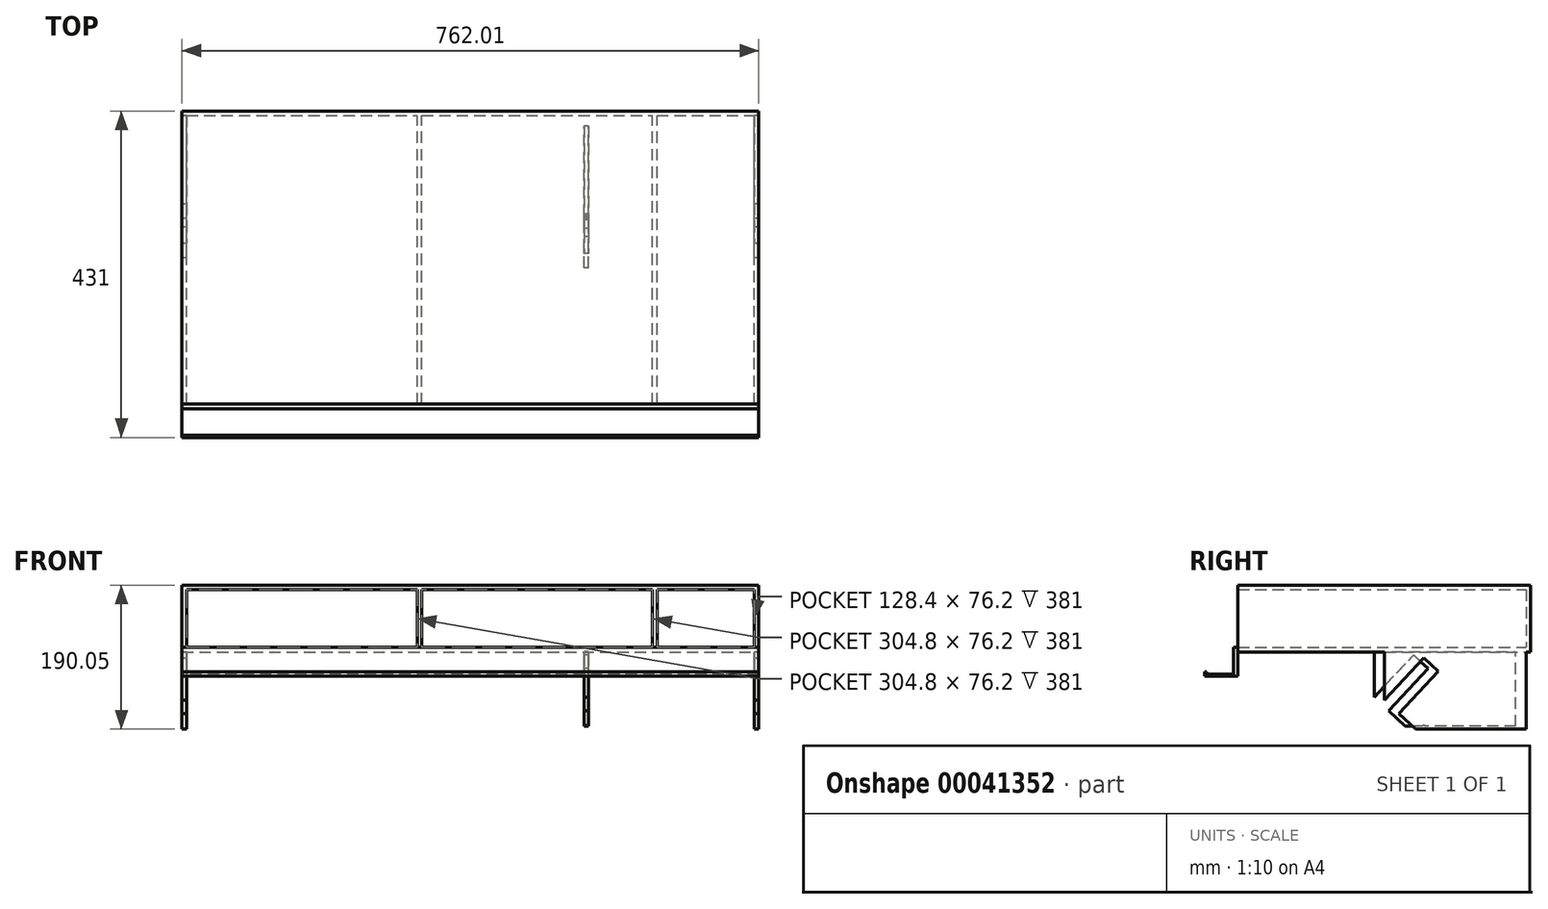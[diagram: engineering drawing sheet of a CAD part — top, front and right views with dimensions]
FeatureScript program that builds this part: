
annotation { "Feature Type Name" : "Feature", "Feature Type Description" : "" }
export const myFeature = defineFeature(function(context is Context, id is Id, definition is map)
    precondition{}
    {
        {
            var Q0;
            Q0=qCreatedBy(makeId("Front.planeOp"),FACE);
            var sketch = newSketch(context, id + "F0", { "sketchPlane" : qUnion([Q0])});
            skLineSegment(sketch, "E0.bottom", {"start": v(-621.6, 86.08) * mm, "end": v(140.4, 86.08) * mm});
            skLineSegment(sketch, "E0.left", {"start": v(-621.6, 86.08) * mm, "end": v(-621.6, 80.08) * mm});
            skLineSegment(sketch, "E0.right", {"start": v(140.4, 86.08) * mm, "end": v(140.4, 80.08) * mm});
            skLineSegment(sketch, "E1.bottom", {"start": v(-621.6, 80.08) * mm, "end": v(-615.6, 80.08) * mm});
            skLineSegment(sketch, "E1.top", {"start": v(-621.6, 3.88) * mm, "end": v(-615.6, 3.88) * mm});
            skLineSegment(sketch, "E1.left", {"start": v(-621.6, 80.08) * mm, "end": v(-621.6, 3.88) * mm});
            skLineSegment(sketch, "E1.right", {"start": v(-615.6, 80.08) * mm, "end": v(-615.6, 3.88) * mm});
            skLineSegment(sketch, "E2.bottom", {"start": v(-621.6, 3.88) * mm, "end": v(140.4, 3.88) * mm});
            skLineSegment(sketch, "E2.top", {"start": v(-621.6, -2.12) * mm, "end": v(140.4, -2.12) * mm});
            skLineSegment(sketch, "E2.left", {"start": v(-621.6, 3.88) * mm, "end": v(-621.6, -2.12) * mm});
            skLineSegment(sketch, "E2.right", {"start": v(140.4, 3.88) * mm, "end": v(140.4, -2.12) * mm});
            skLineSegment(sketch, "E3.bottom", {"start": v(140.4, 80.08) * mm, "end": v(134.4, 80.08) * mm});
            skLineSegment(sketch, "E3.top", {"start": v(140.4, 3.88) * mm, "end": v(134.4, 3.88) * mm});
            skLineSegment(sketch, "E3.left", {"start": v(140.4, 80.08) * mm, "end": v(140.4, 3.88) * mm});
            skLineSegment(sketch, "E3.right", {"start": v(134.4, 80.08) * mm, "end": v(134.4, 3.88) * mm});
            skLineSegment(sketch, "E4.bottom", {"start": v(-304.8, 80.08) * mm, "end": v(-310.8, 80.08) * mm});
            skLineSegment(sketch, "E4.top", {"start": v(-304.8, 3.88) * mm, "end": v(-310.8, 3.88) * mm});
            skLineSegment(sketch, "E4.left", {"start": v(-304.8, 80.08) * mm, "end": v(-304.8, 3.88) * mm});
            skLineSegment(sketch, "E4.right", {"start": v(-310.8, 80.08) * mm, "end": v(-310.8, 3.88) * mm});
            skLineSegment(sketch, "E5.bottom", {"start": v(6, 80.08) * mm, "end": v(0, 80.08) * mm});
            skLineSegment(sketch, "E5.top", {"start": v(6, 3.88) * mm, "end": v(0, 3.88) * mm});
            skLineSegment(sketch, "E5.right", {"start": v(0, 80.08) * mm, "end": v(0, 3.88) * mm});
            skLineSegment(sketch, "E6.bottom", {"start": v(-615.6, 80.08) * mm, "end": v(-310.8, 80.08) * mm});
            skLineSegment(sketch, "E6.top", {"start": v(-615.6, 3.88) * mm, "end": v(-310.8, 3.88) * mm});
            skLineSegment(sketch, "E7.bottom", {"start": v(-304.8, 80.08) * mm, "end": v(0, 80.08) * mm});
            skLineSegment(sketch, "E7.top", {"start": v(-304.8, 3.88) * mm, "end": v(0, 3.88) * mm});
            skLineSegment(sketch, "E8", {"start": v(6, 80.08) * mm, "end": v(6, 3.88) * mm});
            skLineSegment(sketch, "E9", {"start": v(6, 80.08) * mm, "end": v(134.4, 80.08) * mm});
            skSolve(sketch);
        }
        {
            var Q0;
            Q0=makeQuery(id+"F0.imprint","IMPRINT",FACE,{"disambiguationData":[TD([[makeQuery(id+"F0.imprint","IMPRINT",EDGE,{"derivedFrom":sQuery(id+"F0.wireOp",EDGE,"E0.bottom")}),-1.0]])]});
            var Q1;
            Q1=makeQuery(id+"F0.imprint","IMPRINT",FACE,{"disambiguationData":[TD([[makeQuery(id+"F0.imprint","IMPRINT",EDGE,{"derivedFrom":sQuery(id+"F0.wireOp",EDGE,"E4.bottom")}),1.0]])]});
            var Q2;
            Q2=makeQuery(id+"F0.imprint","IMPRINT",FACE,{"disambiguationData":[TD([[makeQuery(id+"F0.imprint","IMPRINT",EDGE,{"derivedFrom":sQuery(id+"F0.wireOp",EDGE,"E5.bottom")}),1.0]])]});
            var Q3;
            Q3=makeQuery(id+"F0.imprint","IMPRINT",FACE,{"disambiguationData":[TD([[makeQuery(id+"F0.imprint","IMPRINT",EDGE,{"derivedFrom":sQuery(id+"F0.wireOp",EDGE,"E2.top")}),1.0]])]});
            var Q4;
            Q4=makeQuery(id+"F0.imprint","IMPRINT",FACE,{"disambiguationData":[TD([[makeQuery(id+"F0.imprint","IMPRINT",EDGE,{"derivedFrom":sQuery(id+"F0.wireOp",EDGE,"E3.bottom")}),1.0]])]});
            var Q5;
            Q5=makeQuery(id+"F0.imprint","IMPRINT",FACE,{"disambiguationData":[TD([[makeQuery(id+"F0.imprint","IMPRINT",EDGE,{"derivedFrom":sQuery(id+"F0.wireOp",EDGE,"E1.bottom")}),-1.0]])]});
            extrude(context, id + "F1", {"entities" : qUnion([Q0, Q1, Q2, Q3, Q4, Q5]), "depth" : 381 * mm});
        }
        {
            var Q0;
            Q0=makeQuery(id+"F1.opExtrude","SWEPT_FACE",FACE,{"disambiguationData":[OSD([sQuery(id+"F0.wireOp",EDGE,"E0.right"),sQuery(id+"F0.wireOp",EDGE,"E2.right"),sQuery(id+"F0.wireOp",EDGE,"E3.left")])]});
            var sketch = newSketch(context, id + "F2", { "sketchPlane" : qUnion([Q0])});
            skLineSegment(sketch, "E10", {"start": v(0, -2.12) * mm, "end": v(-187.2, -2.12) * mm});
            skLineSegment(sketch, "E11", {"start": v(-187.2, -2.12) * mm, "end": v(-187.2, -65.62) * mm});
            skLineSegment(sketch, "E12", {"start": v(-187.2, -65.62) * mm, "end": v(-135.2, -9.92) * mm});
            skLineSegment(sketch, "E13", {"start": v(-135.2, -9.92) * mm, "end": v(-116.08, -27.77) * mm});
            skLineSegment(sketch, "E14", {"start": v(0, -103.97) * mm, "end": v(0, -2.12) * mm});
            skLineSegment(sketch, "E15", {"start": v(-116.08, -27.77) * mm, "end": v(-116.08, -103.97) * mm, "construction": true});
            skLineSegment(sketch, "E16", {"start": v(0, -103.97) * mm, "end": v(-116.08, -103.97) * mm});
            skLineSegment(sketch, "E17", {"start": v(-187.2, -65.62) * mm, "end": v(-168.08, -83.47) * mm, "construction": true});
            skLineSegment(sketch, "E18", {"start": v(-168.08, -83.47) * mm, "end": v(-146.12, -103.97) * mm});
            skLineSegment(sketch, "E19", {"start": v(-116.08, -27.77) * mm, "end": v(-168.08, -83.47) * mm});
            skLineSegment(sketch, "E20", {"start": v(-116.08, -103.97) * mm, "end": v(-146.12, -103.97) * mm});
            skLineSegment(sketch, "E21", {"start": v(-168.08, -83.47) * mm, "end": v(-187.2, -103.97) * mm, "construction": true});
            skLineSegment(sketch, "E22", {"start": v(-187.2, -103.97) * mm, "end": v(-146.12, -103.97) * mm, "construction": true});
            skLineSegment(sketch, "E23", {"start": v(-187.2, -103.97) * mm, "end": v(-116.08, -103.97) * mm, "construction": true});
            skSolve(sketch);
        }
        {
            var Q0;
            Q0 = qSketchRegion(id + "F2", true);
            extrude(context, id + "F3", {"entities" : qUnion([Q0]), "oppositeDirection" : true, "depth" : 6 * mm});
        }
        {
            var Q0;
            Q0=makeQuery(id+"F3.opExtrude","SWEPT_BODY",BODY,{"disambiguationData":[OSD([sQuery(id+"F2.wireOp",EDGE,"E10"),sQuery(id+"F2.wireOp",EDGE,"E11"),sQuery(id+"F2.wireOp",EDGE,"E12"),sQuery(id+"F2.wireOp",EDGE,"E13"),sQuery(id+"F2.wireOp",EDGE,"E14"),sQuery(id+"F2.wireOp",EDGE,"E16"),sQuery(id+"F2.wireOp",EDGE,"E18"),sQuery(id+"F2.wireOp",EDGE,"E19"),sQuery(id+"F2.wireOp",EDGE,"E20")])]});
            transform(context, id + "F4", {"entities" : qUnion([Q0]), "transformType" : TransformType.TRANSLATION_3D, "dx" : -756 * mm, "dy" : 0 * mm, "dz" : 0 * mm, "makeCopy" : true});
        }
        {
            var Q0;
            Q0=makeQuery(id+"F3.opExtrude","SWEPT_BODY",BODY,{"disambiguationData":[OSD([sQuery(id+"F2.wireOp",EDGE,"E10"),sQuery(id+"F2.wireOp",EDGE,"E11"),sQuery(id+"F2.wireOp",EDGE,"E12"),sQuery(id+"F2.wireOp",EDGE,"E13"),sQuery(id+"F2.wireOp",EDGE,"E14"),sQuery(id+"F2.wireOp",EDGE,"E16"),sQuery(id+"F2.wireOp",EDGE,"E18"),sQuery(id+"F2.wireOp",EDGE,"E19"),sQuery(id+"F2.wireOp",EDGE,"E20")])]});
            var Q1;
            Q1=makeQuery(id+"F1.opExtrude","SWEPT_BODY",BODY,{"disambiguationData":[OSD([sQuery(id+"F0.wireOp",EDGE,"E0.bottom"),sQuery(id+"F0.wireOp",EDGE,"E0.left"),sQuery(id+"F0.wireOp",EDGE,"E0.right"),sQuery(id+"F0.wireOp",EDGE,"E1.left"),sQuery(id+"F0.wireOp",EDGE,"E2.bottom"),sQuery(id+"F0.wireOp",EDGE,"E2.top"),sQuery(id+"F0.wireOp",EDGE,"E2.left"),sQuery(id+"F0.wireOp",EDGE,"E2.right"),sQuery(id+"F0.wireOp",EDGE,"E3.left"),sQuery(id+"F0.wireOp",EDGE,"E6.bottom"),sQuery(id+"F0.wireOp",EDGE,"E6.top"),sQuery(id+"F0.wireOp",EDGE,"E1.right"),sQuery(id+"F0.wireOp",EDGE,"E4.right"),sQuery(id+"F0.wireOp",EDGE,"E7.bottom"),sQuery(id+"F0.wireOp",EDGE,"E7.top"),sQuery(id+"F0.wireOp",EDGE,"E4.left"),sQuery(id+"F0.wireOp",EDGE,"E5.right"),sQuery(id+"F0.wireOp",EDGE,"E3.right"),sQuery(id+"F0.wireOp",EDGE,"E8"),sQuery(id+"F0.wireOp",EDGE,"E9")])]});
            booleanBodies(context, id + "F5", {"operationType" : BooleanOperationType.UNION, "tools" : qUnion([Q0, Q1])});
        }
        {
            var Q0;
            Q0=makeQuery(id+"F3.opExtrude","SWEPT_BODY",BODY,{"disambiguationData":[OSD([sQuery(id+"F2.wireOp",EDGE,"E10"),sQuery(id+"F2.wireOp",EDGE,"E11"),sQuery(id+"F2.wireOp",EDGE,"E12"),sQuery(id+"F2.wireOp",EDGE,"E13"),sQuery(id+"F2.wireOp",EDGE,"E14"),sQuery(id+"F2.wireOp",EDGE,"E16"),sQuery(id+"F2.wireOp",EDGE,"E18"),sQuery(id+"F2.wireOp",EDGE,"E19"),sQuery(id+"F2.wireOp",EDGE,"E20")])]});
            var Q1;
            Q1=makeQuery(id+"F4.opPattern","COPY",BODY,{"derivedFrom":makeQuery(id+"F3.opExtrude","SWEPT_BODY",BODY,{"disambiguationData":[OSD([sQuery(id+"F2.wireOp",EDGE,"E10"),sQuery(id+"F2.wireOp",EDGE,"E11"),sQuery(id+"F2.wireOp",EDGE,"E12"),sQuery(id+"F2.wireOp",EDGE,"E13"),sQuery(id+"F2.wireOp",EDGE,"E14"),sQuery(id+"F2.wireOp",EDGE,"E16"),sQuery(id+"F2.wireOp",EDGE,"E18"),sQuery(id+"F2.wireOp",EDGE,"E19"),sQuery(id+"F2.wireOp",EDGE,"E20")])]}),"instanceName":"1"});
            booleanBodies(context, id + "F6", {"operationType" : BooleanOperationType.UNION, "tools" : qUnion([Q0, Q1])});
        }
        {
            var Q0;
            Q0=makeQuery(id+"F5.opBoolean","MERGE",FACE,{"derivedFrom":[makeQuery(id+"F1.opExtrude","SWEPT_FACE",FACE,{"disambiguationData":[OSD([sQuery(id+"F0.wireOp",EDGE,"E0.right"),sQuery(id+"F0.wireOp",EDGE,"E2.right"),sQuery(id+"F0.wireOp",EDGE,"E3.left")])]}),makeQuery(id+"F3.opExtrude","CAP_FACE",FACE,{"disambiguationData":[OSD([sQuery(id+"F2.wireOp",EDGE,"E10"),sQuery(id+"F2.wireOp",EDGE,"E11"),sQuery(id+"F2.wireOp",EDGE,"E12"),sQuery(id+"F2.wireOp",EDGE,"E13"),sQuery(id+"F2.wireOp",EDGE,"E14"),sQuery(id+"F2.wireOp",EDGE,"E16"),sQuery(id+"F2.wireOp",EDGE,"E18"),sQuery(id+"F2.wireOp",EDGE,"E19"),sQuery(id+"F2.wireOp",EDGE,"E20")])],"isStart":true})]});
            var sketch = newSketch(context, id + "F7", { "sketchPlane" : qUnion([Q0])});
            skLineSegment(sketch, "E24", {"start": v(-13.7, 89.62) * mm, "end": v(-200.9, 89.62) * mm});
            skLineSegment(sketch, "E25", {"start": v(-200.9, 89.62) * mm, "end": v(-200.9, 26.12) * mm});
            skLineSegment(sketch, "E26", {"start": v(-200.9, 26.12) * mm, "end": v(-148.91, 81.82) * mm});
            skLineSegment(sketch, "E27", {"start": v(-148.91, 81.82) * mm, "end": v(-129.79, 63.97) * mm});
            skLineSegment(sketch, "E28", {"start": v(-13.7, -12.23) * mm, "end": v(-13.7, 89.62) * mm});
            skLineSegment(sketch, "E29", {"start": v(-129.79, 63.97) * mm, "end": v(-129.79, -12.23) * mm, "construction": true});
            skLineSegment(sketch, "E30", {"start": v(-13.7, -12.23) * mm, "end": v(-129.79, -12.23) * mm});
            skLineSegment(sketch, "E31", {"start": v(-200.9, 26.12) * mm, "end": v(-181.78, 8.27) * mm, "construction": true});
            skLineSegment(sketch, "E32", {"start": v(-181.78, 8.27) * mm, "end": v(-159.83, -12.23) * mm});
            skLineSegment(sketch, "E33", {"start": v(-129.79, 63.97) * mm, "end": v(-181.78, 8.27) * mm});
            skLineSegment(sketch, "E34", {"start": v(-129.79, -12.23) * mm, "end": v(-159.83, -12.23) * mm});
            skLineSegment(sketch, "E35", {"start": v(-181.78, 8.27) * mm, "end": v(-200.9, -12.23) * mm, "construction": true});
            skLineSegment(sketch, "E36", {"start": v(-200.9, -12.23) * mm, "end": v(-159.83, -12.23) * mm, "construction": true});
            skLineSegment(sketch, "E37", {"start": v(-200.9, -12.23) * mm, "end": v(-129.79, -12.23) * mm, "construction": true});
            skSolve(sketch);
        }
        {
            var Q0;
            {var subQ11=sQuery(id+"F7.wireOp",EDGE,"E26");Q0=makeQuery(id+"F7.imprint","IMPRINT",FACE,{"disambiguationData":[TD([[makeQuery(id+"F7.imprint","IMPRINT",EDGE,{"derivedFrom":subQ11}),1.0]])]});}
            extrude(context, id + "F8", {"entities" : qUnion([Q0]), "depth" : 6 * mm});
        }
        {
            var Q0;
            Q0=makeQuery(id+"F8.opExtrude","SWEPT_BODY",BODY,{"disambiguationData":[OSD([sQuery(id+"F0.wireOp",EDGE,"E0.bottom"),sQuery(id+"F0.wireOp",EDGE,"E0.right"),sQuery(id+"F2.wireOp",EDGE,"E12"),sQuery(id+"F2.wireOp",EDGE,"E13"),sQuery(id+"F7.wireOp",EDGE,"E25"),sQuery(id+"F7.wireOp",EDGE,"E26"),sQuery(id+"F7.wireOp",EDGE,"E27"),sQuery(id+"F7.wireOp",EDGE,"E28"),sQuery(id+"F7.wireOp",EDGE,"E30"),sQuery(id+"F7.wireOp",EDGE,"E32"),sQuery(id+"F7.wireOp",EDGE,"E33"),sQuery(id+"F7.wireOp",EDGE,"E34")])]});
            transform(context, id + "F9", {"entities" : qUnion([Q0]), "transformType" : TransformType.TRANSLATION_3D, "dx" : -230.88 * mm, "dy" : 0 * mm, "dz" : -87.98 * mm, "makeCopy" : false});
        }
        {
            var Q0;
            Q0=makeQuery(id+"F1.opExtrude","SWEPT_FACE",FACE,{"disambiguationData":[OSD([sQuery(id+"F0.wireOp",EDGE,"E0.bottom")])]});
            var sketch = newSketch(context, id + "F10", { "sketchPlane" : qUnion([Q0])});
            skLineSegment(sketch, "E38.bottom", {"start": v(140.4, 0) * mm, "end": v(-621.6, 0) * mm});
            skLineSegment(sketch, "E38.top", {"start": v(140.4, 6) * mm, "end": v(-621.6, 6) * mm});
            skLineSegment(sketch, "E38.left", {"start": v(140.4, 0) * mm, "end": v(140.4, 6) * mm});
            skLineSegment(sketch, "E38.right", {"start": v(-621.6, 0) * mm, "end": v(-621.6, 6) * mm});
            skSolve(sketch);
        }
        {
            var Q0;
            Q0 = qSketchRegion(id + "F10", true);
            var Q1;
            Q1=makeQuery(id+"F1.opExtrude","SWEPT_FACE",FACE,{"disambiguationData":[OSD([sQuery(id+"F0.wireOp",EDGE,"E2.top")])]});
            extrude(context, id + "F11", {"entities" : qUnion([Q0]), "operationType" : NewBodyOperationType.ADD, "endBound" : BoundingType.UP_TO_SURFACE, "oppositeDirection" : true, "endBoundEntityFace" : qUnion([Q1]), "depth" : 25.4 * mm});
        }
        {
            var Q0;
            Q0=makeQuery(id+"F11.boolean.opBoolean","MERGE",FACE,{"derivedFrom":[makeQuery(id+"F1.opExtrude","SWEPT_FACE",FACE,{"disambiguationData":[OSD([sQuery(id+"F0.wireOp",EDGE,"E0.left"),sQuery(id+"F0.wireOp",EDGE,"E1.left"),sQuery(id+"F0.wireOp",EDGE,"E2.left")])]}),makeQuery(id+"F11.opExtrude","SWEPT_FACE",FACE,{"disambiguationData":[OSD([sQuery(id+"F10.wireOp",EDGE,"E38.right")])]})]});
            var sketch = newSketch(context, id + "F12", { "sketchPlane" : qUnion([Q0])});
            skLineSegment(sketch, "E39", {"start": v(381, -2.12) * mm, "end": v(381, -37.22) * mm});
            skLineSegment(sketch, "E40", {"start": v(381, -37.22) * mm, "end": v(416, -37.22) * mm});
            skLineSegment(sketch, "E41", {"start": v(416, -37.22) * mm, "end": v(416, -34.22) * mm});
            skLineSegment(sketch, "E42", {"start": v(416, -34.22) * mm, "end": v(419, -34.22) * mm});
            skLineSegment(sketch, "E43", {"start": v(419, -34.22) * mm, "end": v(419, -40.22) * mm});
            skLineSegment(sketch, "E44", {"start": v(419, -40.22) * mm, "end": v(375, -40.22) * mm});
            skLineSegment(sketch, "E45", {"start": v(375, -40.22) * mm, "end": v(375, -2.12) * mm});
            skLineSegment(sketch, "E46", {"start": v(375, -2.12) * mm, "end": v(381, -2.12) * mm});
            skLineSegment(sketch, "E47", {"start": v(381, -37.22) * mm, "end": v(381, -40.22) * mm, "construction": true});
            skLineSegment(sketch, "E48", {"start": v(419, -37.22) * mm, "end": v(419, -40.22) * mm, "construction": true});
            skSolve(sketch);
        }
        {
            var Q0;
            Q0=makeQuery(id+"F12.imprint","IMPRINT",FACE,{"disambiguationData":[TD([[makeQuery(id+"F12.imprint","IMPRINT",EDGE,{"derivedFrom":sQuery(id+"F12.wireOp",EDGE,"E39")}),-1.0]])]});
            var Q1;
            Q1=makeQuery(id+"F11.boolean.opBoolean","MERGE",FACE,{"derivedFrom":[makeQuery(id+"F5.opBoolean","MERGE",FACE,{"derivedFrom":[makeQuery(id+"F1.opExtrude","SWEPT_FACE",FACE,{"disambiguationData":[OSD([sQuery(id+"F0.wireOp",EDGE,"E0.right"),sQuery(id+"F0.wireOp",EDGE,"E2.right"),sQuery(id+"F0.wireOp",EDGE,"E3.left")])]}),makeQuery(id+"F3.opExtrude","CAP_FACE",FACE,{"disambiguationData":[OSD([sQuery(id+"F2.wireOp",EDGE,"E10"),sQuery(id+"F2.wireOp",EDGE,"E11"),sQuery(id+"F2.wireOp",EDGE,"E12"),sQuery(id+"F2.wireOp",EDGE,"E13"),sQuery(id+"F2.wireOp",EDGE,"E14"),sQuery(id+"F2.wireOp",EDGE,"E16"),sQuery(id+"F2.wireOp",EDGE,"E18"),sQuery(id+"F2.wireOp",EDGE,"E19"),sQuery(id+"F2.wireOp",EDGE,"E20")])],"isStart":true})]}),makeQuery(id+"F11.opExtrude","SWEPT_FACE",FACE,{"disambiguationData":[OSD([sQuery(id+"F10.wireOp",EDGE,"E38.left")])]})]});
            extrude(context, id + "F13", {"entities" : qUnion([Q0]), "endBound" : BoundingType.UP_TO_SURFACE, "oppositeDirection" : true, "endBoundEntityFace" : qUnion([Q1]), "depth" : 25.4 * mm});
        }
        {
            var Q0;
            Q0=makeQuery(id+"F13.opExtrude","SWEPT_BODY",BODY,{"disambiguationData":[OSD([sQuery(id+"F12.wireOp",EDGE,"E39"),sQuery(id+"F12.wireOp",EDGE,"E40"),sQuery(id+"F12.wireOp",EDGE,"E41"),sQuery(id+"F12.wireOp",EDGE,"E42"),sQuery(id+"F12.wireOp",EDGE,"E43"),sQuery(id+"F12.wireOp",EDGE,"E44"),sQuery(id+"F12.wireOp",EDGE,"E45"),sQuery(id+"F12.wireOp",EDGE,"E46")])]});
            transform(context, id + "F14", {"entities" : qUnion([Q0]), "transformType" : TransformType.TRANSLATION_3D, "dx" : 0 * mm, "dy" : -6 * mm, "dz" : 6 * mm, "makeCopy" : false});
        }
    });
